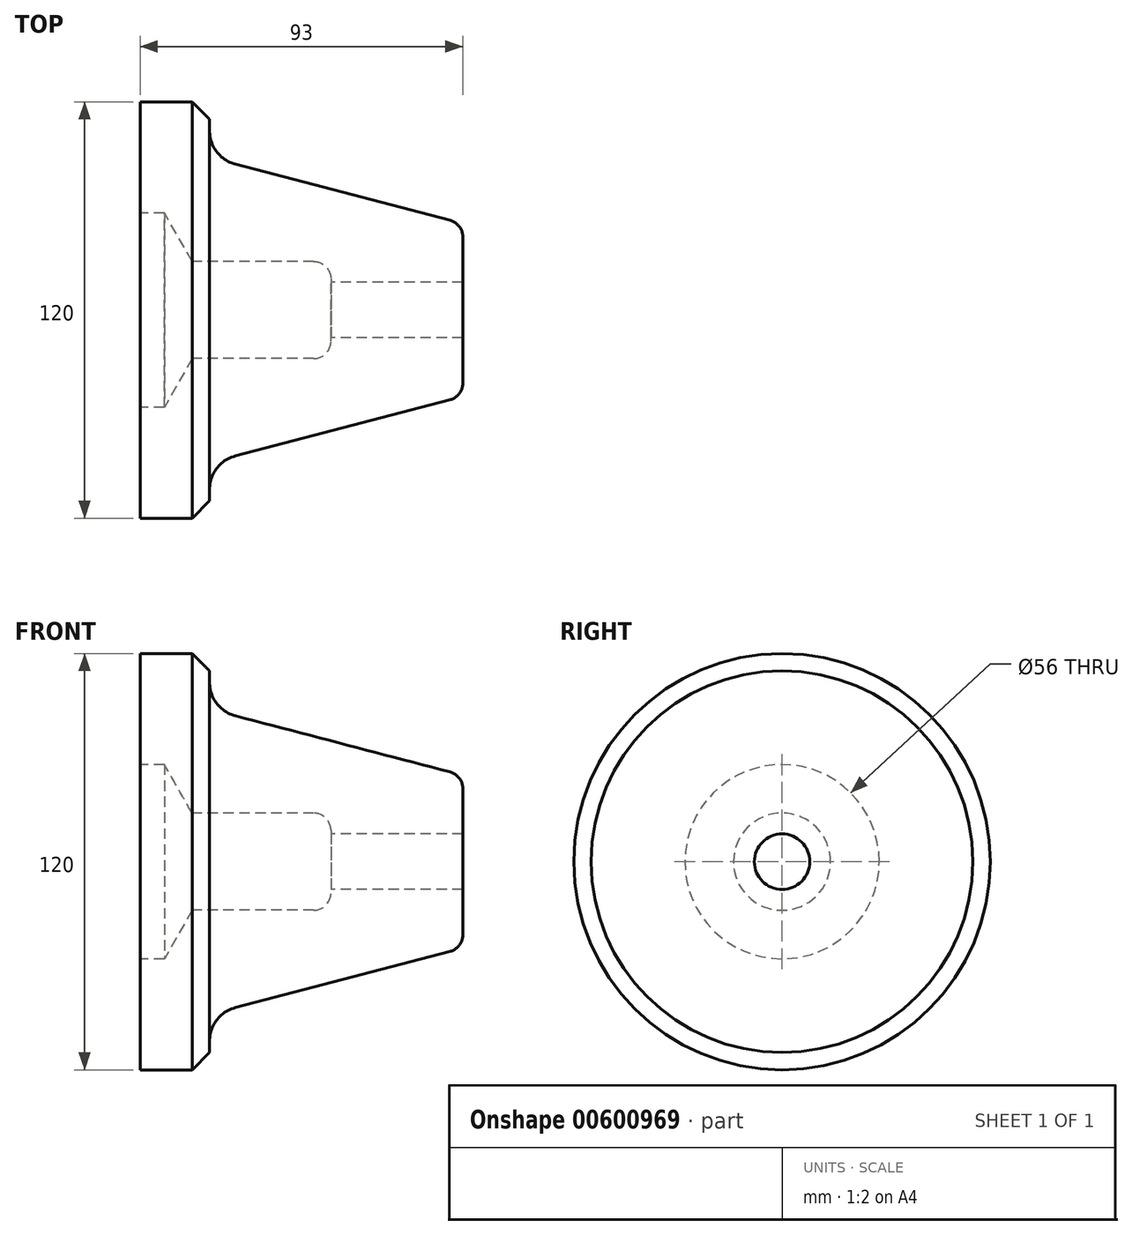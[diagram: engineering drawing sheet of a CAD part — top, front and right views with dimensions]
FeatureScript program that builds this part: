
annotation { "Feature Type Name" : "Feature", "Feature Type Description" : "" }
export const myFeature = defineFeature(function(context is Context, id is Id, definition is map)
    precondition{}
    {
        {
            var Q0;
            Q0=qCreatedBy(makeId("Front.planeOp"),FACE);
            var sketch = newSketch(context, id + "F0", { "sketchPlane" : qUnion([Q0])});
            skLineSegment(sketch, "E0", {"start": v(93, 8) * mm, "end": v(93, 24.9) * mm});
            skLineSegment(sketch, "E1", {"start": v(93, 24.9) * mm, "end": v(20, 44) * mm});
            skLineSegment(sketch, "E2", {"start": v(20, 44) * mm, "end": v(20, 55) * mm});
            skLineSegment(sketch, "E3", {"start": v(20, 55) * mm, "end": v(15, 60) * mm});
            skLineSegment(sketch, "E4", {"start": v(15, 60) * mm, "end": v(0, 60) * mm});
            skLineSegment(sketch, "E5", {"start": v(0, 60) * mm, "end": v(0, 28) * mm});
            skLineSegment(sketch, "E6", {"start": v(93, 8) * mm, "end": v(55, 8) * mm});
            skLineSegment(sketch, "E7", {"start": v(55, 8) * mm, "end": v(55, 14) * mm});
            skLineSegment(sketch, "E8", {"start": v(55, 14) * mm, "end": v(15, 14) * mm});
            skLineSegment(sketch, "E9", {"start": v(15, 14) * mm, "end": v(7, 28) * mm});
            skLineSegment(sketch, "E10", {"start": v(7, 28) * mm, "end": v(0, 28) * mm});
            skPoint(sketch, "E11.orphan", {"position": v(0, 0) * mm});
            skLineSegment(sketch, "E12", {"start": v(0, 0) * mm, "end": v(108.78, 0) * mm, "construction": true});
            skSolve(sketch);
        }
        {
            var Q0;
            Q0 = qSketchRegion(id + "F0", true);
            var Q1;
            Q1=sQuery(id+"F0.wireOp",EDGE,"E12");
            revolve(context, id + "F1", {"entities" : qUnion([Q0]), "axis" : qUnion([Q1]), "revolveType" : RevolveType.FULL});
        }
        {
            var Q0;
            Q0=makeQuery(id+"F1.opRevolve","SWEPT_EDGE",EDGE,{"disambiguationData":[OSD([sQuery(id+"F0.wireOp",EDGE,"E0"),sQuery(id+"F0.wireOp",EDGE,"E1")])]});
            fillet(context, id + "F2", {"entities" : qUnion([Q0]), "radius" : 5 * mm, "tangentPropagation" : true, "allowEdgeOverflow" : false});
        }
        {
            var Q0;
            Q0=makeQuery(id+"F1.opRevolve","SWEPT_EDGE",EDGE,{"disambiguationData":[OSD([sQuery(id+"F0.wireOp",EDGE,"E1"),sQuery(id+"F0.wireOp",EDGE,"E2")])]});
            fillet(context, id + "F3", {"entities" : qUnion([Q0]), "radius" : 10 * mm, "tangentPropagation" : true, "allowEdgeOverflow" : false});
        }
        {
            var Q0;
            Q0=makeQuery(id+"F1.opRevolve","SWEPT_EDGE",EDGE,{"disambiguationData":[OSD([sQuery(id+"F0.wireOp",EDGE,"E7"),sQuery(id+"F0.wireOp",EDGE,"E8")])]});
            fillet(context, id + "F4", {"entities" : qUnion([Q0]), "radius" : 5 * mm, "tangentPropagation" : true, "allowEdgeOverflow" : false});
        }
    });
